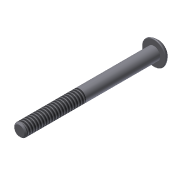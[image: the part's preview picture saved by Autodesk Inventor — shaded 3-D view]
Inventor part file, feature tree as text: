
AUTODESK INVENTOR PART (.ipt)
format: ipt  version: 2013 (Build 170138000, 138)  size: 115,200 bytes
history: native  units: in
note: dims shown in document units (in); Inventor stores cm internally (conversion verified against a paired STEP export)
features: sketch x3, extrude x2, revolve x1, chamfer x1, thread x1
ambient origin geometry x8: Origin, YZ Plane, XZ Plane, XY Plane, X Axis, Y Axis, Z Axis, Center Point
bodies: Solid1 (feature_tree)
feature tree (8):
  extrude  "Extrusion1"  Depth=2.0in TaperAngle=0.0deg
  revolve  "Revolution1"  [1 undecoded]
  extrude  "Extrusion2"  Depth=0.125in
  chamfer  "Chamfer1"  Distance=0.0625in
  thread  "Thread2"  [1 undecoded]
  sketch  "Sketch1"  dims[d0=0.19in d1=2.0in d2=0.0in]
  sketch  "Sketch2"  dims[d3=0.101in d6=0.08in]
  sketch  "Sketch3"  dims[d7=90.0deg d8=0.125in d9=0.0625in d10=0.0in d12=0.1805in d13=0.02in d14=0.125in d15=45.0deg d18=0.875in d19=0.0in]
note: 2 required parameter values undecoded (feature->parameter linkage not recoverable at this tier; creation-order binding heuristic only, values carry confidence <= 0.55)